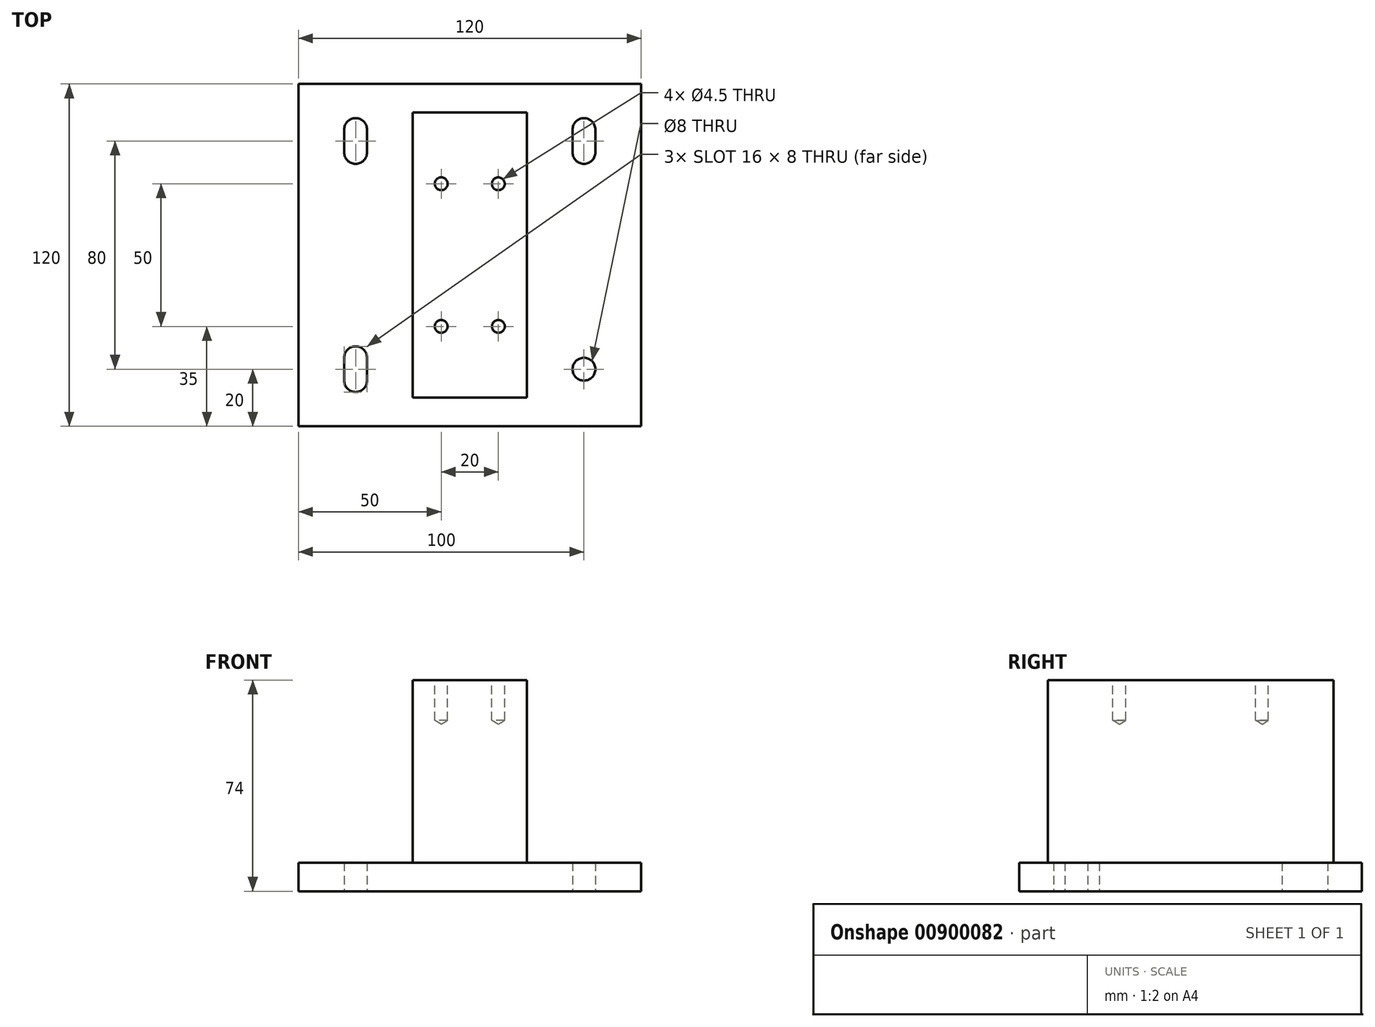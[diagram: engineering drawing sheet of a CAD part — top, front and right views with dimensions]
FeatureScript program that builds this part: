
annotation { "Feature Type Name" : "Feature", "Feature Type Description" : "" }
export const myFeature = defineFeature(function(context is Context, id is Id, definition is map)
    precondition{}
    {
        {
            var Q0;
            Q0=qCreatedBy(makeId("Top.planeOp"),FACE);
            var sketch = newSketch(context, id + "F0", { "sketchPlane" : qUnion([Q0])});
            skLineSegment(sketch, "E0.bottom", {"start": v(20, -50) * mm, "end": v(-20, -50) * mm});
            skLineSegment(sketch, "E0.top", {"start": v(20, 50) * mm, "end": v(-20, 50) * mm});
            skLineSegment(sketch, "E0.left", {"start": v(20, -50) * mm, "end": v(20, 50) * mm});
            skLineSegment(sketch, "E0.right", {"start": v(-20, -50) * mm, "end": v(-20, 50) * mm});
            skPoint(sketch, "E0.middle", {"position": v(0, 0) * mm});
            skLineSegment(sketch, "E1.bottom", {"start": v(10, -25) * mm, "end": v(-10, -25) * mm, "construction": true});
            skLineSegment(sketch, "E1.top", {"start": v(10, 25) * mm, "end": v(-10, 25) * mm, "construction": true});
            skLineSegment(sketch, "E1.left", {"start": v(10, -25) * mm, "end": v(10, 25) * mm, "construction": true});
            skLineSegment(sketch, "E1.right", {"start": v(-10, -25) * mm, "end": v(-10, 25) * mm, "construction": true});
            skLineSegment(sketch, "E2.bottom", {"start": v(60, -60) * mm, "end": v(-60, -60) * mm});
            skLineSegment(sketch, "E2.top", {"start": v(60, 60) * mm, "end": v(-60, 60) * mm});
            skLineSegment(sketch, "E2.left", {"start": v(60, -60) * mm, "end": v(60, 60) * mm});
            skLineSegment(sketch, "E2.right", {"start": v(-60, -60) * mm, "end": v(-60, 60) * mm});
            skSolve(sketch);
        }
        {
            var Q0;
            Q0=makeQuery(id+"F0.imprint","IMPRINT",FACE,{"disambiguationData":[TD([[makeQuery(id+"F0.imprint","IMPRINT",EDGE,{"derivedFrom":sQuery(id+"F0.wireOp",EDGE,"E0.bottom")}),-1.0]])]});
            extrude(context, id + "F1", {"entities" : qUnion([Q0]), "oppositeDirection" : true, "depth" : 64 * mm, "offsetDistance" : 25 * mm});
        }
        {
            var Q0;
            Q0=sQuery(id+"F0.wireOp",VERTEX,"E1.top.end");
            var Q1;
            Q1=sQuery(id+"F0.wireOp",VERTEX,"E1.top.start");
            var Q2;
            Q2=sQuery(id+"F0.wireOp",VERTEX,"E1.bottom.end");
            var Q3;
            Q3=sQuery(id+"F0.wireOp",VERTEX,"E1.bottom.start");
            var Q4;
            Q4=makeQuery(id+"F1.opExtrude","SWEPT_BODY",BODY,{"disambiguationData":[OSD([sQuery(id+"F0.wireOp",EDGE,"E0.bottom"),sQuery(id+"F0.wireOp",EDGE,"E0.top"),sQuery(id+"F0.wireOp",EDGE,"E0.left"),sQuery(id+"F0.wireOp",EDGE,"E0.right")])]});
            hole(context, id + "F2", {"style" : HoleStyle.SIMPLE, "endStyle" : HoleEndStyle.BLIND, "standardTappedOrClearance" : lookupTablePath({ "fit" : "Normal", "standard" : "ISO", "size" : "M4", "type" : "Clearance" }), "standardBlindInLast" : lookupTablePath({ "fit" : "Normal", "standard" : "ISO", "size" : "M4", "type" : "Clearance" }), "holeDiameter" : 4.5 * mm, "majorDiameter" : 4 * mm, "holeDepth" : 14.1 * mm, "tappedDepth" : 12 * mm, "tapClearance" : 3, "startFromSketch" : true, "locations" : qUnion([Q0, Q1, Q2, Q3]), "scope" : qUnion([Q4])});
        }
        {
            var Q0;
            Q0=makeQuery(id+"F0.imprint","IMPRINT",FACE,{"disambiguationData":[TD([[makeQuery(id+"F0.imprint","IMPRINT",EDGE,{"derivedFrom":sQuery(id+"F0.wireOp",EDGE,"E0.bottom")}),1.0]])]});
            var Q1;
            Q1=makeQuery(id+"F0.imprint","IMPRINT",FACE,{"disambiguationData":[TD([[makeQuery(id+"F0.imprint","IMPRINT",EDGE,{"derivedFrom":sQuery(id+"F0.wireOp",EDGE,"E0.bottom")}),-1.0]])]});
            var Q2;
            Q2=makeQuery(id+"F1.opExtrude","CAP_FACE",FACE,{"disambiguationData":[OSD([sQuery(id+"F0.wireOp",EDGE,"E0.bottom"),sQuery(id+"F0.wireOp",EDGE,"E0.top"),sQuery(id+"F0.wireOp",EDGE,"E0.left"),sQuery(id+"F0.wireOp",EDGE,"E0.right")])],"isStart":false});
            extrude(context, id + "F3", {"entities" : qUnion([Q0, Q1]), "oppositeDirection" : true, "depth" : 74 * mm, "offsetDistance" : 25 * mm, "hasSecondDirection" : true, "secondDirectionBound" : SecondDirectionBoundingType.UP_TO_SURFACE, "secondDirectionOppositeDirection" : true, "secondDirectionDepth" : 68 * mm, "secondDirectionBoundEntityFace" : qUnion([Q2])});
        }
        {
            var Q0;
            Q0=makeQuery(id+"F3.opExtrude","CAP_FACE",FACE,{"disambiguationData":[OSD([sQuery(id+"F0.wireOp",EDGE,"E2.bottom"),sQuery(id+"F0.wireOp",EDGE,"E2.top"),sQuery(id+"F0.wireOp",EDGE,"E2.left"),sQuery(id+"F0.wireOp",EDGE,"E2.right")])],"isStart":false});
            var sketch = newSketch(context, id + "F4", { "sketchPlane" : qUnion([Q0])});
            skLineSegment(sketch, "E3.bottom", {"start": v(40, -40) * mm, "end": v(-40, -40) * mm, "construction": true});
            skLineSegment(sketch, "E3.top", {"start": v(40, 40) * mm, "end": v(-40, 40) * mm, "construction": true});
            skLineSegment(sketch, "E3.left", {"start": v(40, -40) * mm, "end": v(40, 40) * mm, "construction": true});
            skLineSegment(sketch, "E3.right", {"start": v(-40, -40) * mm, "end": v(-40, 40) * mm, "construction": true});
            skPoint(sketch, "E3.middle", {"position": v(0, 0) * mm});
            skCircle(sketch, "E4", {"center": v(40, 40) * mm, "radius": 4 * mm});
            skCircle(sketch, "E5", {"center": v(40, -36) * mm, "radius": 4 * mm});
            skCircle(sketch, "E6", {"center": v(40, -44) * mm, "radius": 4 * mm});
            skCircle(sketch, "E7", {"center": v(-40, -36) * mm, "radius": 4 * mm});
            skCircle(sketch, "E8", {"center": v(-40, -44) * mm, "radius": 4 * mm});
            skCircle(sketch, "E9", {"center": v(-40, 44) * mm, "radius": 4 * mm});
            skCircle(sketch, "E10", {"center": v(-40, 36) * mm, "radius": 4 * mm});
            skLineSegment(sketch, "E11", {"start": v(-44, 44) * mm, "end": v(-44, 36) * mm});
            skLineSegment(sketch, "E12", {"start": v(-36, 44) * mm, "end": v(-36, 36) * mm});
            skLineSegment(sketch, "E13", {"start": v(-44, -36) * mm, "end": v(-44, -44) * mm});
            skLineSegment(sketch, "E14", {"start": v(-36, -36) * mm, "end": v(-36, -44) * mm});
            skLineSegment(sketch, "E15", {"start": v(36, -36) * mm, "end": v(36, -44) * mm});
            skLineSegment(sketch, "E16", {"start": v(44, -36) * mm, "end": v(44, -44) * mm});
            skSolve(sketch);
        }
        {
            var Q0;
            {var subQ0=sQuery(id+"F4.wireOp",EDGE,"E9");var subQ1=makeQuery(id+"F4.imprint","INTERSECT",VERTEX,{"derivedFrom":[subQ0,sQuery(id+"F4.wireOp",EDGE,"E11")]});Q0=makeQuery(id+"F4.imprint","IMPRINT",FACE,{"disambiguationData":[TD([[makeQuery(id+"F4.imprint","IMPRINT",EDGE,{"disambiguationData":[TD([[subQ1,1.0]])],"derivedFrom":subQ0}),1.0]])]});}
            var Q1;
            {var subQ0=sQuery(id+"F4.wireOp",EDGE,"E10");var subQ1=makeQuery(id+"F4.imprint","INTERSECT",VERTEX,{"derivedFrom":[subQ0,sQuery(id+"F4.wireOp",EDGE,"E12")]});Q1=makeQuery(id+"F4.imprint","IMPRINT",FACE,{"disambiguationData":[TD([[makeQuery(id+"F4.imprint","IMPRINT",EDGE,{"disambiguationData":[TD([[subQ1,-1.0]])],"derivedFrom":subQ0}),1.0]])]});}
            var Q2;
            {var subQ0=sQuery(id+"F4.wireOp",EDGE,"E12");Q2=makeQuery(id+"F4.imprint","IMPRINT",FACE,{"disambiguationData":[TD([[makeQuery(id+"F4.imprint","IMPRINT",EDGE,{"derivedFrom":subQ0}),-1.0]])]});}
            var Q3;
            {var subQ0=sQuery(id+"F4.wireOp",EDGE,"E11");Q3=makeQuery(id+"F4.imprint","IMPRINT",FACE,{"disambiguationData":[TD([[makeQuery(id+"F4.imprint","IMPRINT",EDGE,{"derivedFrom":subQ0}),1.0]])]});}
            var Q4;
            Q4=makeQuery(id+"F4.imprint","IMPRINT",FACE,{"disambiguationData":[TD([[makeQuery(id+"F4.imprint","IMPRINT",EDGE,{"derivedFrom":sQuery(id+"F4.wireOp",EDGE,"E4")}),1.0]])]});
            var Q5;
            {var subQ0=sQuery(id+"F4.wireOp",EDGE,"E7");var subQ1=makeQuery(id+"F4.imprint","INTERSECT",VERTEX,{"derivedFrom":[subQ0,sQuery(id+"F4.wireOp",EDGE,"E13")]});Q5=makeQuery(id+"F4.imprint","IMPRINT",FACE,{"disambiguationData":[TD([[makeQuery(id+"F4.imprint","IMPRINT",EDGE,{"disambiguationData":[TD([[subQ1,1.0]])],"derivedFrom":subQ0}),1.0]])]});}
            var Q6;
            {var subQ0=sQuery(id+"F4.wireOp",EDGE,"E8");var subQ1=makeQuery(id+"F4.imprint","INTERSECT",VERTEX,{"derivedFrom":[subQ0,sQuery(id+"F4.wireOp",EDGE,"E14")]});Q6=makeQuery(id+"F4.imprint","IMPRINT",FACE,{"disambiguationData":[TD([[makeQuery(id+"F4.imprint","IMPRINT",EDGE,{"disambiguationData":[TD([[subQ1,-1.0]])],"derivedFrom":subQ0}),1.0]])]});}
            var Q7;
            {var subQ0=sQuery(id+"F4.wireOp",EDGE,"E13");Q7=makeQuery(id+"F4.imprint","IMPRINT",FACE,{"disambiguationData":[TD([[makeQuery(id+"F4.imprint","IMPRINT",EDGE,{"derivedFrom":subQ0}),1.0]])]});}
            var Q8;
            {var subQ0=sQuery(id+"F4.wireOp",EDGE,"E14");Q8=makeQuery(id+"F4.imprint","IMPRINT",FACE,{"disambiguationData":[TD([[makeQuery(id+"F4.imprint","IMPRINT",EDGE,{"derivedFrom":subQ0}),-1.0]])]});}
            var Q9;
            {var subQ0=sQuery(id+"F4.wireOp",EDGE,"E6");var subQ1=makeQuery(id+"F4.imprint","INTERSECT",VERTEX,{"derivedFrom":[subQ0,sQuery(id+"F4.wireOp",EDGE,"E16")]});Q9=makeQuery(id+"F4.imprint","IMPRINT",FACE,{"disambiguationData":[TD([[makeQuery(id+"F4.imprint","IMPRINT",EDGE,{"disambiguationData":[TD([[subQ1,-1.0]])],"derivedFrom":subQ0}),1.0]])]});}
            var Q10;
            {var subQ0=sQuery(id+"F4.wireOp",EDGE,"E5");var subQ1=makeQuery(id+"F4.imprint","INTERSECT",VERTEX,{"derivedFrom":[subQ0,sQuery(id+"F4.wireOp",EDGE,"E15")]});Q10=makeQuery(id+"F4.imprint","IMPRINT",FACE,{"disambiguationData":[TD([[makeQuery(id+"F4.imprint","IMPRINT",EDGE,{"disambiguationData":[TD([[subQ1,1.0]])],"derivedFrom":subQ0}),1.0]])]});}
            var Q11;
            {var subQ0=sQuery(id+"F4.wireOp",EDGE,"E15");Q11=makeQuery(id+"F4.imprint","IMPRINT",FACE,{"disambiguationData":[TD([[makeQuery(id+"F4.imprint","IMPRINT",EDGE,{"derivedFrom":subQ0}),1.0]])]});}
            var Q12;
            {var subQ0=sQuery(id+"F4.wireOp",EDGE,"E16");Q12=makeQuery(id+"F4.imprint","IMPRINT",FACE,{"disambiguationData":[TD([[makeQuery(id+"F4.imprint","IMPRINT",EDGE,{"derivedFrom":subQ0}),-1.0]])]});}
            extrude(context, id + "F5", {"entities" : qUnion([Q0, Q1, Q2, Q3, Q4, Q5, Q6, Q7, Q8, Q9, Q10, Q11, Q12]), "operationType" : NewBodyOperationType.REMOVE, "oppositeDirection" : true, "depth" : 25 * mm, "offsetDistance" : 25 * mm});
        }
    });
